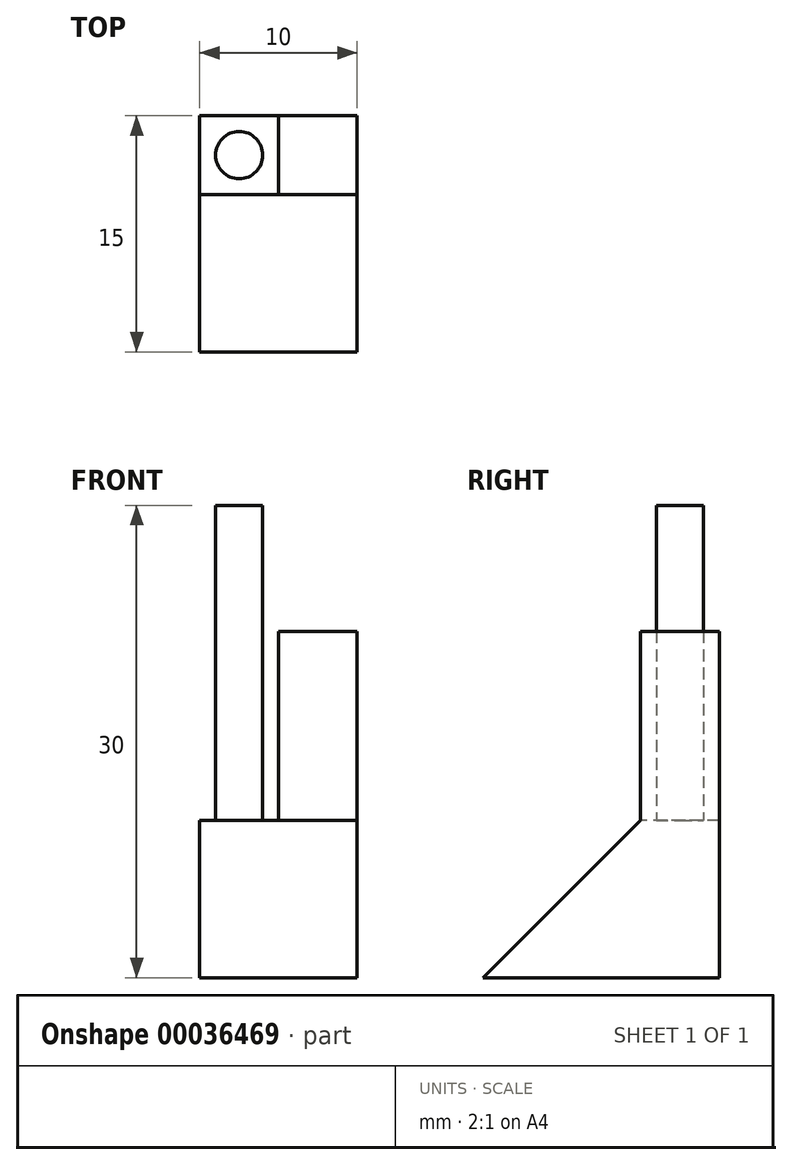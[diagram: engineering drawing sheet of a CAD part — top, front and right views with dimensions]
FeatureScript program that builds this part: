
annotation { "Feature Type Name" : "Feature", "Feature Type Description" : "" }
export const myFeature = defineFeature(function(context is Context, id is Id, definition is map)
    precondition{}
    {
        {
            var Q0;
            Q0=qCreatedBy(makeId("Top.planeOp"),FACE);
            var sketch = newSketch(context, id + "F0", { "sketchPlane" : qUnion([Q0])});
            skLineSegment(sketch, "E0.rect.bottom", {"start": v(5, 7.5) * mm, "end": v(-5, 7.5) * mm});
            skLineSegment(sketch, "E0.rect.top", {"start": v(5, -7.5) * mm, "end": v(-5, -7.5) * mm});
            skLineSegment(sketch, "E0.rect.left", {"start": v(5, 7.5) * mm, "end": v(5, -7.5) * mm});
            skLineSegment(sketch, "E0.rect.right", {"start": v(-5, 7.5) * mm, "end": v(-5, -7.5) * mm});
            skPoint(sketch, "E0.rect.middle", {"position": v(0, 0) * mm});
            skSolve(sketch);
        }
        {
            var Q0;
            Q0=makeQuery(id+"F0.imprint","IMPRINT",FACE,{"disambiguationData":[TD([[makeQuery(id+"F0.imprint","IMPRINT",EDGE,{"derivedFrom":sQuery(id+"F0.wireOp",EDGE,"E0.rect.bottom")}),1.0]])]});
            extrude(context, id + "F1", {"entities" : qUnion([Q0]), "depth" : 10 * mm});
        }
        {
            var Q0;
            Q0=makeQuery(id+"F1.opExtrude","CAP_FACE",FACE,{"disambiguationData":[OSD([sQuery(id+"F0.wireOp",EDGE,"E0.rect.bottom"),sQuery(id+"F0.wireOp",EDGE,"E0.rect.top"),sQuery(id+"F0.wireOp",EDGE,"E0.rect.left"),sQuery(id+"F0.wireOp",EDGE,"E0.rect.right")])],"isStart":false});
            var sketch = newSketch(context, id + "F2", { "sketchPlane" : qUnion([Q0])});
            skLineSegment(sketch, "E1.bottom", {"start": v(5, 7.5) * mm, "end": v(0, 7.5) * mm});
            skLineSegment(sketch, "E1.top", {"start": v(5, 2.5) * mm, "end": v(0, 2.5) * mm});
            skLineSegment(sketch, "E1.left", {"start": v(5, 7.5) * mm, "end": v(5, 2.5) * mm});
            skLineSegment(sketch, "E1.right", {"start": v(0, 7.5) * mm, "end": v(0, 2.5) * mm});
            skSolve(sketch);
        }
        {
            var Q0;
            Q0 = qSketchRegion(id + "F2", true);
            extrude(context, id + "F3", {"entities" : qUnion([Q0]), "operationType" : NewBodyOperationType.ADD, "depth" : 12 * mm});
        }
        {
            var Q0;
            Q0=makeQuery(id+"F1.opExtrude","CAP_FACE",FACE,{"disambiguationData":[OSD([sQuery(id+"F0.wireOp",EDGE,"E0.rect.bottom"),sQuery(id+"F0.wireOp",EDGE,"E0.rect.top"),sQuery(id+"F0.wireOp",EDGE,"E0.rect.left"),sQuery(id+"F0.wireOp",EDGE,"E0.rect.right")])],"isStart":false});
            var sketch = newSketch(context, id + "F4", { "sketchPlane" : qUnion([Q0])});
            skCircle(sketch, "E2", {"center": v(-2.5, 5) * mm, "radius": 1.5 * mm});
            skSolve(sketch);
        }
        {
            var Q0;
            Q0 = qSketchRegion(id + "F4", true);
            extrude(context, id + "F5", {"entities" : qUnion([Q0]), "operationType" : NewBodyOperationType.ADD, "depth" : 20 * mm});
        }
        {
            var Q0;
            Q0=makeQuery(id+"F3.boolean.opBoolean","MERGE",FACE,{"derivedFrom":[makeQuery(id+"F1.opExtrude","SWEPT_FACE",FACE,{"disambiguationData":[OSD([sQuery(id+"F0.wireOp",EDGE,"E0.rect.left")])]}),makeQuery(id+"F3.opExtrude","SWEPT_FACE",FACE,{"disambiguationData":[OSD([sQuery(id+"F2.wireOp",EDGE,"E1.left")])]})]});
            var sketch = newSketch(context, id + "F6", { "sketchPlane" : qUnion([Q0])});
            skLineSegment(sketch, "E3", {"start": v(-7.5, 0) * mm, "end": v(2.5, 10) * mm});
            skLineSegment(sketch, "E4", {"start": v(2.5, 10) * mm, "end": v(-7.5, 10) * mm});
            skLineSegment(sketch, "E5", {"start": v(-7.5, 10) * mm, "end": v(-7.5, 0) * mm});
            skSolve(sketch);
        }
        {
            var Q0;
            Q0=makeQuery(id+"F6.imprint","IMPRINT",FACE,{"disambiguationData":[TD([[makeQuery(id+"F6.imprint","IMPRINT",EDGE,{"derivedFrom":sQuery(id+"F6.wireOp",EDGE,"E3")}),1.0]])]});
            extrude(context, id + "F7", {"entities" : qUnion([Q0]), "operationType" : NewBodyOperationType.REMOVE, "oppositeDirection" : true, "depth" : 10 * mm});
        }
    });
